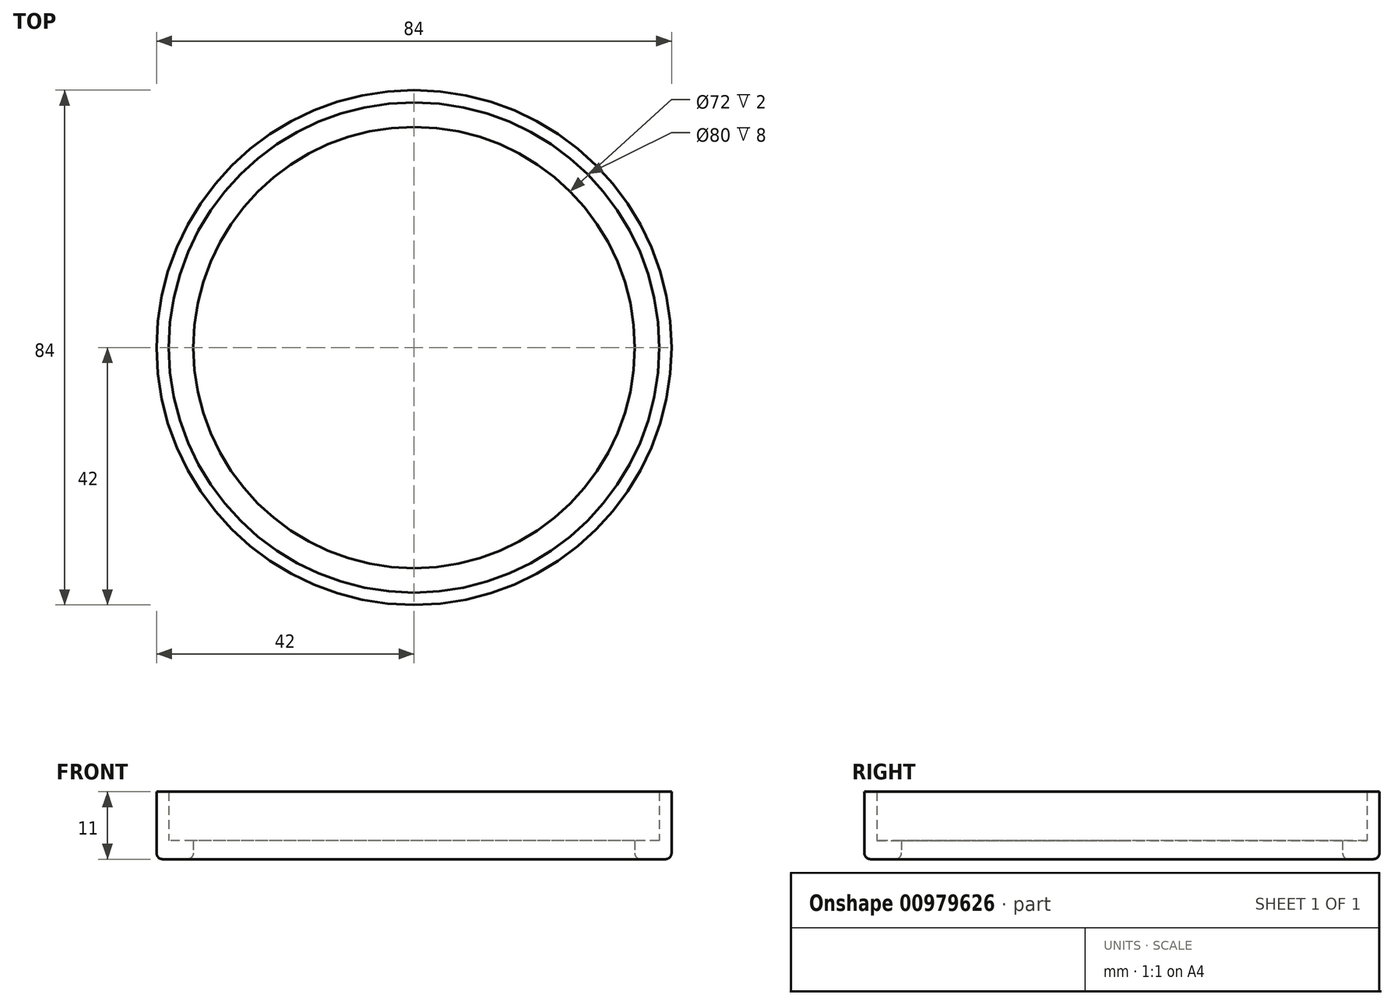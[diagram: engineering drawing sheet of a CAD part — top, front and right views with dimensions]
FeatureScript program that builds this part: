
annotation { "Feature Type Name" : "Feature", "Feature Type Description" : "" }
export const myFeature = defineFeature(function(context is Context, id is Id, definition is map)
    precondition{}
    {
        {
            var Q0;
            Q0=qCreatedBy(makeId("Top.planeOp"),FACE);
            var sketch = newSketch(context, id + "F0", { "sketchPlane" : qUnion([Q0])});
            skCircle(sketch, "E0", {"center": v(0, 0) * mm, "radius": 42 * mm});
            skCircle(sketch, "E1", {"center": v(0, 0) * mm, "radius": 40 * mm});
            skCircle(sketch, "E2", {"center": v(0, 0) * mm, "radius": 36 * mm});
            skSolve(sketch);
        }
        {
            var Q0;
            Q0=makeQuery(id+"F0.imprint","IMPRINT",FACE,{"disambiguationData":[TD([[makeQuery(id+"F0.imprint","IMPRINT",EDGE,{"derivedFrom":sQuery(id+"F0.wireOp",EDGE,"E1")}),1.0]])]});
            extrude(context, id + "F1", {"entities" : qUnion([Q0]), "depth" : 3 * mm, "offsetDistance" : 25 * mm});
        }
        {
            var Q0;
            Q0=makeQuery(id+"F0.imprint","IMPRINT",FACE,{"disambiguationData":[TD([[makeQuery(id+"F0.imprint","IMPRINT",EDGE,{"derivedFrom":sQuery(id+"F0.wireOp",EDGE,"E0")}),1.0]])]});
            extrude(context, id + "F2", {"entities" : qUnion([Q0]), "operationType" : NewBodyOperationType.ADD, "depth" : 11 * mm, "offsetDistance" : 25 * mm});
        }
        {
            var Q0;
            Q0=makeQuery(id+"F2.opExtrude","CAP_EDGE",EDGE,{"disambiguationData":[OSD([sQuery(id+"F0.wireOp",EDGE,"E0")])],"isStart":true});
            fillet(context, id + "F3", {"entities" : qUnion([Q0]), "radius" : 1 * mm, "tangentPropagation" : true, "allowEdgeOverflow" : false});
        }
        {
            var Q0;
            Q0=makeQuery(id+"F1.opExtrude","CAP_EDGE",EDGE,{"disambiguationData":[OSD([sQuery(id+"F0.wireOp",EDGE,"E2")])],"isStart":true});
            fillet(context, id + "F4", {"entities" : qUnion([Q0]), "radius" : 1 * mm, "tangentPropagation" : true, "allowEdgeOverflow" : false});
        }
    });
